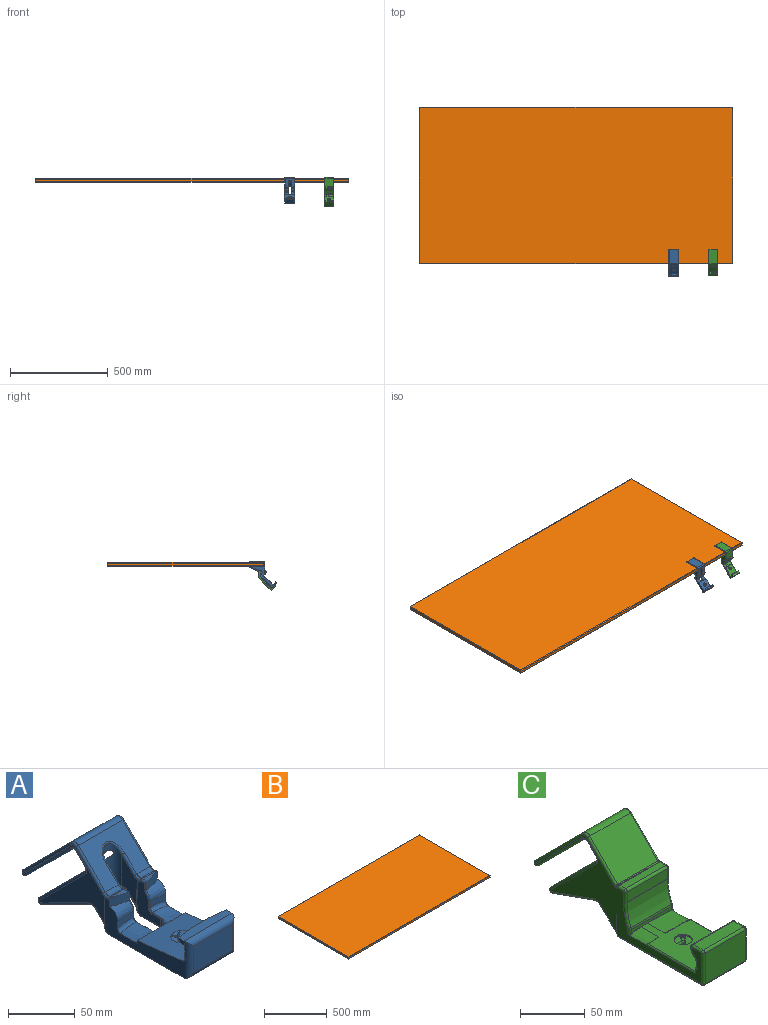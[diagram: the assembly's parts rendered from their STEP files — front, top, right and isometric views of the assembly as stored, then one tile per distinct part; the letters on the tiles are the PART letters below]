
ASSEMBLY  parts=3 mates=2
PART A: 157 faces, bbox 58x178.3x75.5 mm
  f0: plane 46.81x28.52mm, normal (0,-0.71,0.71), area 1310.9mm2, adj f93,f95,f96,f110,f126,f151,f152,f154
  f1: plane 22.07x1.36mm, normal (0,-1,-0.05), area 4.8mm2, adj f3,f60,f61,f104,f141
  f2: plane 13.46x10.49mm, normal (0,0.71,-0.71), area 199.8mm2, adj f4,f13,f140,f141
  f3: bspline ~5.22x5.21mm, area 0.6mm2, adj f1,f60,f104,f148,f149,f150
  f4: cylinder r=5mm len=13.6mm, axis (-1,0,0), area 84mm2, adj f2,f84,f139,f142,f143
  f5: cylinder r=3mm len=18.91mm, axis (1,0,0), area 89.1mm2, adj f86,f87,f103,f117
  f6: extruded ~23.2x17.5mm, area 327.6mm2, adj f14,f26,f31,f32,f46,f50,f80,f82
  f7: plane 14.8x4.53mm, normal (0,0,1), area 40.9mm2, adj f8,f12,f125,f148
  f8: cylinder r=64.23mm len=16.24mm, axis (0,0,-1), area 138mm2, adj f7,f10,f27,f64,f125,f148
  f9: plane 16.39x7.94mm, normal (0,-1,0), area 91.5mm2, adj f10,f11,f27,f68
  f10: bspline ~24.3x9.47mm, area 179.2mm2, adj f8,f9,f27,f64,f66
  f11: bspline ~21.12x6.05mm, area 78.8mm2, adj f9,f27,f30,f70
  f12: cylinder r=5mm len=14.56mm, axis (1,0,0), area 18.3mm2, adj f7,f95,f125,f149
  f13: cylinder r=5mm len=16.38mm, axis (-1,0,0), area 129.8mm2, adj f2,f25,f27,f61,f62,f140,f141
  f14: extruded ~50.8x50.75mm, area 2434.9mm2, adj f6,f15,f16,f17,f24,f26,f27,f28
  f15: extruded ~11.38x4.58mm, area 51.7mm2, adj f14,f16,f25,f55,f57
  f16: extruded ~11.38x4.58mm, area 51.7mm2, adj f14,f15,f25,f54,f57
  f17: extruded ~11.41x3.75mm, area 45.5mm2, adj f14,f18,f25,f54,f56
  f18: extruded ~10.43x9mm, area 95.8mm2, adj f17,f19,f25,f56
  f19: cylinder r=7.6mm len=10.43mm, axis (0,0,1), area 5mm2, adj f18,f20,f25,f56
  f20: extruded ~10.4x7.96mm, area 89.4mm2, adj f19,f21,f25,f56
  f21: extruded ~10.4x7.96mm, area 89.4mm2, adj f20,f22,f25,f56
  f22: cylinder r=7.6mm len=10.43mm, axis (0,0,1), area 5mm2, adj f21,f23,f25,f56
  f23: extruded ~10.43x9mm, area 95.8mm2, adj f22,f24,f25,f56
  f24: extruded ~11.41x3.75mm, area 45.5mm2, adj f14,f23,f25,f55,f56
  f25: plane 79x50.8mm, normal (0,0,-1), area 3479.4mm2, adj f13,f15,f16,f17,f18,f19,f20,f21
  f26: plane 84.61x32.41mm, normal (1,0,0), area 1122.5mm2, adj f6,f14,f25,f29,f31,f44,f45,f49
  f27: plane 84.61x32.68mm, normal (-1,0,0), area 1124.1mm2, adj f8,f9,f10,f11,f13,f14,f25,f28
  f28: cylinder r=5mm len=34mm, axis (0,0,-1), area 229mm2, adj f14,f27,f36,f38,f39,f40,f41,f42
  f29: cylinder r=5mm len=34mm, axis (0,0,1), area 230mm2, adj f14,f26,f35,f38,f39,f40,f41,f42
  f30: extruded ~23.06x17.5mm, area 322.8mm2, adj f11,f14,f27,f32,f33,f48,f72,f73
  f31: plane 12.47x2.53mm, normal (0,1,0), area 9.5mm2, adj f6,f14,f26
  f32: plane 19.29x7.26mm, normal (0,1,0), area 76.8mm2, adj f6,f14,f30,f78
  f33: plane 12.3x2.44mm, normal (0,1,0), area 9.3mm2, adj f14,f27,f30
  f34: plane 13.6x4.54mm, normal (0,0,1), area 40.4mm2, adj f44,f51,f106,f153
  f35: plane 6.51x4.26mm, normal (1,0,0), area 20mm2, adj f29,f37,f38,f43
  f36: plane 6.55x4.26mm, normal (-1,0,0), area 20.2mm2, adj f28,f37,f38,f43
  f37: plane 50.8x8.41mm, normal (0,0,1), area 390.9mm2, adj f35,f36,f41,f43
  f38: plane 50.8x4.13mm, normal (0,0,-1), area 65.1mm2, adj f28,f29,f35,f36,f42,f43
  f39: plane 40.8x24mm, normal (0,-1,0), area 979.2mm2, adj f28,f29,f40,f41
  f40: cylinder r=5mm len=50.8mm, axis (1,0,0), area 359.7mm2, adj f25,f28,f29,f39
  f41: cylinder r=5mm len=50.8mm, axis (-1,0,0), area 359.7mm2, adj f28,f29,f37,f39
  f42: cylinder r=105.29mm len=50.73mm, axis (0,0,-1), area 518.6mm2, adj f28,f29,f38,f47,f53
  f43: torus R=147.23mm, axis (0,0,1), area 350.7mm2, adj f35,f36,f37,f38
  f44: cylinder r=64.23mm len=16.38mm, axis (0,0,-1), area 138.9mm2, adj f26,f34,f49,f75,f106,f153
  f45: plane 16.54x8.04mm, normal (0,-1,0), area 92.4mm2, adj f26,f49,f50,f79
  f46: plane 4.06x0.18mm, normal (0,-1,0), area 0.2mm2, adj f6,f14
  f47: plane 35.45x1.5mm, normal (0,0,-1), area 35.6mm2, adj f42,f53
  f48: plane 3.97x0.13mm, normal (0,-1,0), area 0.2mm2, adj f14,f30
  f49: bspline ~22.57x10.34mm, area 180.9mm2, adj f26,f44,f45,f75,f77
  f50: bspline ~20.53x5.8mm, area 79.7mm2, adj f6,f26,f45,f81
  f51: cylinder r=5mm len=13.6mm, axis (1,0,0), area 17.8mm2, adj f34,f93,f107,f155
  f52: cylinder r=5mm len=16.52mm, axis (-1,0,0), area 130.9mm2, adj f25,f26,f69,f71,f91,f124,f147
  f53: cylinder r=2mm len=50.73mm, axis (1,0,0), area 146.4mm2, adj f14,f28,f29,f42,f47
  f54: cylinder r=7.6mm len=11.41mm, axis (0,0,1), area 5.8mm2, adj f14,f16,f17,f25
  f55: cylinder r=7.6mm len=11.41mm, axis (0,0,1), area 5.8mm2, adj f14,f15,f24,f25
  f56: sphere r=12.32mm, area 242.2mm2, adj f14,f17,f18,f19,f20,f21,f22,f23
  f57: sphere r=12.32mm, area 14.4mm2, adj f14,f15,f16
  f58: plane 31.56x24.67mm, normal (-1,0,0), area 419.9mm2, adj f59,f67,f69,f71,f75,f77,f79,f81
  f59: cylinder r=7.95mm len=15.91mm, axis (0,0,1), area 104.9mm2, adj f58,f60,f65,f73,f76,f78,f80
  f60: plane 31.57x24.52mm, normal (1,0,0), area 419.3mm2, adj f1,f3,f59,f61,f62,f63,f64,f66
  f61: cylinder r=1mm len=18.79mm, axis (0,0,-1), area 10.8mm2, adj f1,f13,f60,f62,f141
  f62: torus R=4mm, axis (1,0,0), area 11.3mm2, adj f13,f60,f61,f63
  f63: cylinder r=1mm len=20.52mm, axis (0,-1,0), area 32.2mm2, adj f25,f60,f62,f65
  f64: cylinder r=1mm len=8.61mm, axis (0,0,-1), area 13mm2, adj f8,f10,f60,f66,f148
  f65: torus R=8.95mm, axis (0,0,-1), area 41.3mm2, adj f25,f59,f63,f67
  f66: bspline ~10.43x6.27mm, area 14.2mm2, adj f10,f60,f64,f68
  f67: cylinder r=1mm len=20.67mm, axis (0,1,0), area 32.5mm2, adj f25,f58,f65,f69
  f68: cylinder r=1mm len=5.89mm, axis (0,0,1), area 9.3mm2, adj f9,f60,f66,f70
  f69: torus R=4mm, axis (1,0,0), area 11.3mm2, adj f52,f58,f67,f71
  f70: bspline ~4.97x4.87mm, area 7.7mm2, adj f11,f60,f68,f72
  f71: cylinder r=1mm len=18.79mm, axis (0,0,1), area 10.8mm2, adj f52,f58,f69,f90,f147
  f72: cylinder r=1mm len=8.77mm, axis (0,-1,0), area 11.1mm2, adj f30,f60,f70,f73
  f73: bspline ~3.21x1.13mm, area 3.2mm2, adj f30,f59,f72,f74
  f74: bspline ~0.78x0.33mm, area 0mm2, adj f30,f73,f76
  f75: cylinder r=1mm len=8.61mm, axis (0,0,-1), area 13mm2, adj f44,f49,f58,f77,f153
  f76: bspline ~7.06x6.68mm, area 10.2mm2, adj f30,f59,f74,f78
  f77: bspline ~10.43x6.27mm, area 14.2mm2, adj f49,f58,f75,f79
  f78: bspline ~5.28x1.44mm, area 5.8mm2, adj f32,f59,f76,f80
  f79: cylinder r=1mm len=5.9mm, axis (0,0,-1), area 9.3mm2, adj f45,f58,f77,f81
  f80: bspline ~9.19x7.2mm, area 13.4mm2, adj f6,f59,f78,f82
  f81: bspline ~5.03x4.86mm, area 7.5mm2, adj f50,f58,f79,f82
  f82: cylinder r=1mm len=8.92mm, axis (0,-1,0), area 10.5mm2, adj f6,f58,f80,f81
  f83: plane 87.64x70.47mm, normal (1,0,0), area 1316.6mm2, adj f26,f109,f110,f111,f112,f113,f114,f115
  f84: plane 51.38x46.81mm, normal (0,-0.44,-0.9), area 2551.5mm2, adj f4,f97,f98,f122,f138,f144
  f85: plane 46.81x0.5mm, normal (0,0.71,-0.71), area 32.9mm2, adj f98,f99,f120,f136
  f86: plane 49.14x49.14mm, normal (0,0.71,0.71), area 3240.2mm2, adj f5,f99,f101,f103,f118,f134
  f87: plane 46.81x9.19mm, normal (0,0.71,-0.71), area 595.7mm2, adj f5,f101,f102,f103,f116,f132
  f88: plane 49.14x49.14mm, normal (0,-0.71,-0.71), area 3252.9mm2, adj f100,f102,f114,f130
  f89: plane 51.27x51.27mm, normal (0,0.71,0.71), area 3393.4mm2, adj f96,f100,f112,f128
  f90: plane 22.07x1.35mm, normal (0,-1,-0.05), area 4.8mm2, adj f58,f71,f94,f105,f147
  f91: plane 13.6x10.49mm, normal (0,0.71,-0.71), area 201.8mm2, adj f52,f97,f124,f147
  f92: plane 87.63x70.47mm, normal (-1,0,0), area 1316.6mm2, adj f27,f125,f126,f127,f128,f129,f130,f131
  f93: cylinder r=5mm len=13.6mm, axis (1,0,0), area 71.2mm2, adj f0,f51,f108,f109,f156
  f94: bspline ~5.21x5.19mm, area 0.6mm2, adj f58,f90,f105,f153,f155,f156
  f95: cylinder r=5mm len=13.46mm, axis (1,0,0), area 70.5mm2, adj f0,f12,f125,f150
  f96: cylinder r=5mm len=46.81mm, axis (-1,0,0), area 367.6mm2, adj f0,f89,f111,f127
  f97: cylinder r=5mm len=13.75mm, axis (-1,0,0), area 84.9mm2, adj f84,f91,f123,f145,f146
  f98: cylinder r=2.5mm len=46.81mm, axis (-1,0,0), area 145.9mm2, adj f84,f85,f121,f137
  f99: cylinder r=2.5mm len=46.81mm, axis (-1,0,0), area 183.8mm2, adj f85,f86,f119,f135
  f100: cylinder r=2.5mm len=46.81mm, axis (1,0,0), area 367.6mm2, adj f88,f89,f113,f129
  f101: cylinder r=3mm len=18.77mm, axis (1,0,0), area 88.4mm2, adj f86,f87,f103,f133
  f102: cylinder r=3mm len=46.81mm, axis (1,0,0), area 220.6mm2, adj f87,f88,f115,f131
  f103: cylinder r=7.87mm len=42.38mm, axis (0,0,-1), area 853.5mm2, adj f5,f86,f87,f101,f104,f105,f143,f144
  f104: plane 38.69x19.09mm, normal (1,0,0), area 387.2mm2, adj f1,f3,f103,f141,f142,f143,f150,f151
  f105: plane 38.94x19.33mm, normal (-1,0,0), area 394.1mm2, adj f90,f94,f103,f146,f147,f154,f156
  f106: cylinder r=2mm len=2mm, axis (0,-1,0), area 1.1mm2, adj f26,f34,f44,f107
  f107: torus R=3mm, axis (-1,0,0), area 3.5mm2, adj f26,f51,f106,f108
  f108: torus R=7mm, axis (-1,0,0), area 8.7mm2, adj f26,f93,f107,f109
  f109: torus R=7mm, axis (1,0,0), area 10.2mm2, adj f83,f93,f108,f110
  f110: cylinder r=2mm len=29.94mm, axis (0,0.71,0.71), area 126.7mm2, adj f0,f83,f109,f111
  f111: torus R=3mm, axis (1,0,0), area 21.1mm2, adj f83,f96,f110,f112
  f112: cylinder r=2mm len=52.68mm, axis (0,0.71,-0.71), area 227.8mm2, adj f83,f89,f111,f113
  f113: torus R=0.5mm, axis (1,0,0), area 17.5mm2, adj f83,f100,f112,f114
  f114: cylinder r=2mm len=50.56mm, axis (0,-0.71,0.71), area 218.3mm2, adj f83,f88,f113,f115
  f115: torus R=5mm, axis (1,0,0), area 18.4mm2, adj f83,f102,f114,f116
  f116: cylinder r=2mm len=10.61mm, axis (0,-0.71,-0.71), area 40.8mm2, adj f83,f87,f115,f117
  f117: torus R=5mm, axis (1,0,0), area 18.4mm2, adj f5,f83,f116,f118
  f118: cylinder r=2mm len=50.56mm, axis (0,0.71,-0.71), area 218.3mm2, adj f83,f86,f117,f119
  f119: torus R=0.5mm, axis (1,0,0), area 8.8mm2, adj f83,f99,f118,f120
  f120: cylinder r=2mm len=2mm, axis (0,-0.71,-0.71), area 2.2mm2, adj f83,f85,f119,f121
  f121: torus R=0.5mm, axis (1,0,0), area 6.9mm2, adj f83,f98,f120,f122
  f122: cylinder r=2mm len=52.27mm, axis (0,-0.9,0.44), area 180.2mm2, adj f83,f84,f121,f123
  f123: torus R=7mm, axis (1,0,0), area 22.4mm2, adj f83,f97,f122,f124
  f124: cylinder r=2mm len=11.91mm, axis (0,-0.71,-0.71), area 44.6mm2, adj f26,f52,f83,f91,f123
  f125: torus R=7mm, axis (1,0,0), area 22.1mm2, adj f7,f8,f12,f27,f92,f95,f126
  f126: cylinder r=2mm len=29.94mm, axis (0,-0.71,-0.71), area 126.7mm2, adj f0,f92,f125,f127
  f127: torus R=3mm, axis (1,0,0), area 21.1mm2, adj f92,f96,f126,f128
  f128: cylinder r=2mm len=52.68mm, axis (0,-0.71,0.71), area 227.8mm2, adj f89,f92,f127,f129
  f129: torus R=0.5mm, axis (1,0,0), area 17.5mm2, adj f92,f100,f128,f130
  f130: cylinder r=2mm len=50.56mm, axis (0,0.71,-0.71), area 218.3mm2, adj f88,f92,f129,f131
  f131: torus R=5mm, axis (1,0,0), area 18.4mm2, adj f92,f102,f130,f132
  f132: cylinder r=2mm len=10.61mm, axis (0,0.71,0.71), area 40.8mm2, adj f87,f92,f131,f133
  f133: torus R=5mm, axis (1,0,0), area 18.4mm2, adj f92,f101,f132,f134
  f134: cylinder r=2mm len=50.56mm, axis (0,-0.71,0.71), area 218.3mm2, adj f86,f92,f133,f135
  f135: torus R=0.5mm, axis (1,0,0), area 8.8mm2, adj f92,f99,f134,f136
  f136: cylinder r=2mm len=2mm, axis (0,0.71,0.71), area 2.2mm2, adj f85,f92,f135,f137
  f137: torus R=0.5mm, axis (1,0,0), area 6.9mm2, adj f92,f98,f136,f138
  f138: cylinder r=2mm len=52.27mm, axis (0,0.9,-0.44), area 180.2mm2, adj f84,f92,f137,f139
  f139: torus R=7mm, axis (1,0,0), area 22.4mm2, adj f4,f92,f138,f140
  f140: cylinder r=2mm len=11.91mm, axis (0,0.71,0.71), area 44.7mm2, adj f2,f13,f27,f92,f139
  f141: cylinder r=2mm len=11.91mm, axis (0,-0.71,-0.71), area 44.4mm2, adj f1,f2,f13,f61,f104,f142
  f142: torus R=7mm, axis (1,0,0), area 17.1mm2, adj f4,f104,f141,f143
  f143: bspline ~3.89x3.13mm, area 4.6mm2, adj f4,f103,f104,f142,f144
  f144: bspline ~19.46x8.22mm, area 65.2mm2, adj f84,f103,f143,f145
  f145: bspline ~3.77x3.13mm, area 3.9mm2, adj f97,f103,f144,f146
  f146: torus R=7mm, axis (1,0,0), area 17.8mm2, adj f97,f105,f145,f147
  f147: cylinder r=2mm len=11.91mm, axis (0,0.71,0.71), area 44.4mm2, adj f52,f71,f90,f91,f105,f146
  f148: cylinder r=2mm len=4.66mm, axis (0,1,0), area 11.5mm2, adj f3,f7,f8,f60,f64,f149
  f149: torus R=3mm, axis (1,0,0), area 3.3mm2, adj f3,f12,f148,f150
  f150: torus R=7mm, axis (1,0,0), area 18.8mm2, adj f3,f95,f104,f149,f151
  f151: cylinder r=2mm len=14.07mm, axis (0,0.71,0.71), area 56.2mm2, adj f0,f104,f150,f152
  f152: bspline ~19.75x13mm, area 79.3mm2, adj f0,f103,f104,f151,f154
  f153: cylinder r=2mm len=4.67mm, axis (0,-1,0), area 11.5mm2, adj f34,f44,f58,f75,f94,f155
  f154: cylinder r=2mm len=14.33mm, axis (0,-0.71,-0.71), area 57.4mm2, adj f0,f105,f152,f156
  f155: torus R=3mm, axis (1,0,0), area 3.3mm2, adj f51,f94,f153,f156
  f156: torus R=7mm, axis (1,0,0), area 18.8mm2, adj f93,f94,f105,f154,f155
PART B: 26 faces, bbox 1600x800x19 mm
  f0: plane 1594x13mm, normal (0,1,0), area 20722mm2, adj f14,f19,f22,f25
  f1: plane 794x13mm, normal (-1,0,0), area 10322mm2, adj f11,f20,f21,f25
  f2: plane 1594x13mm, normal (0,-1,0), area 20722mm2, adj f6,f10,f11,f12
  f3: plane 794x13mm, normal (1,0,0), area 10322mm2, adj f6,f9,f13,f14
  f4: plane 1594x794mm, normal (0,0,1), area 1265636mm2, adj f9,f10,f19,f20
  f5: plane 1594x794mm, normal (0,0,-1), area 1265636mm2, adj f12,f13,f21,f22
  f6: cylinder r=3mm len=13mm, axis (0,0,1), area 61.3mm2, adj f2,f3,f7,f8
  f7: sphere r=3mm, area 14.1mm2, adj f6,f9,f10
  f8: sphere r=3mm, area 14.1mm2, adj f6,f12,f13
  f9: cylinder r=3mm len=794mm, axis (0,-1,0), area 3741.6mm2, adj f3,f4,f7,f15
  f10: cylinder r=3mm len=1594mm, axis (-1,0,0), area 7511.5mm2, adj f2,f4,f7,f16
  f11: cylinder r=3mm len=13mm, axis (0,0,-1), area 61.3mm2, adj f1,f2,f16,f17
  f12: cylinder r=3mm len=1594mm, axis (1,0,0), area 7511.5mm2, adj f2,f5,f8,f17
  f13: cylinder r=3mm len=794mm, axis (0,1,0), area 3741.6mm2, adj f3,f5,f8,f18
  f14: cylinder r=3mm len=13mm, axis (0,0,-1), area 61.3mm2, adj f0,f3,f15,f18
  f15: sphere r=3mm, area 14.1mm2, adj f9,f14,f19
  f16: sphere r=3mm, area 14.1mm2, adj f10,f11,f20
  f17: sphere r=3mm, area 14.1mm2, adj f11,f12,f21
  f18: sphere r=3mm, area 14.1mm2, adj f13,f14,f22
  f19: cylinder r=3mm len=1594mm, axis (1,0,0), area 7511.5mm2, adj f0,f4,f15,f23
  f20: cylinder r=3mm len=794mm, axis (0,1,0), area 3741.6mm2, adj f1,f4,f16,f23
  f21: cylinder r=3mm len=794mm, axis (0,-1,0), area 3741.6mm2, adj f1,f5,f17,f24
  f22: cylinder r=3mm len=1594mm, axis (-1,0,0), area 7511.5mm2, adj f0,f5,f18,f24
  f23: sphere r=3mm, area 14.1mm2, adj f19,f20,f25
  f24: sphere r=3mm, area 14.1mm2, adj f21,f22,f25
  f25: cylinder r=3mm len=13mm, axis (0,0,1), area 61.3mm2, adj f0,f1,f23,f24
PART C: 152 faces, bbox 49.5x185.6x80.7 mm
  f0: cylinder r=2mm len=45.04mm, axis (-1,0,0), area 43.4mm2, adj f6,f66,f69,f111,f141,f151
  f1: plane 43.83x2.19mm, normal (0,1,0), area 96.1mm2, adj f29,f47,f53,f56
  f2: plane 93.01x44.56mm, normal (1,0,0), area 1119.8mm2, adj f11,f12,f13,f20,f21,f23,f26,f34
  f3: plane 93x44.55mm, normal (-1,0,0), area 1142.3mm2, adj f14,f15,f16,f18,f19,f22,f26,f43
  f4: plane 43.83x28.98mm, normal (0,-1,0), area 1270mm2, adj f41,f42,f49,f50
  f5: extruded ~71.8x46.09mm, area 2417.4mm2, adj f9,f10,f12,f13,f14,f15,f18,f19
  f6: plane 43.83x6.31mm, normal (0,0,1), area 276.7mm2, adj f0,f66,f69,f70
  f7: plane 91x43.83mm, normal (0,0,-1), area 3988.2mm2, adj f36,f39,f42,f43
  f8: plane 43.83x0.05mm, normal (0,1,0), area 2.4mm2, adj f39,f110,f115,f127
  f9: plane 45.9x3.61mm, normal (0,1,0), area 133.9mm2, adj f5,f26,f77,f78
  f10: plane 43.9x3.29mm, normal (0,-1,0), area 118.1mm2, adj f5,f32,f62,f76
  f11: plane 1.61x1.13mm, normal (0,1,0), area 0.6mm2, adj f2,f13,f21
  f12: plane 28.53x3.08mm, normal (0,-1,0), area 4.6mm2, adj f2,f5,f13,f23
  f13: extruded ~28.45x19.1mm, area 539.2mm2, adj f2,f5,f11,f12,f21
  f14: extruded ~19.1x12.61mm, area 241.5mm2, adj f3,f5,f15,f16,f19
  f15: plane 12.68x1.87mm, normal (0,-1,0), area 1.6mm2, adj f3,f5,f14,f22
  f16: plane 0.06x0.04mm, normal (0,1,0), area 0mm2, adj f3,f14,f19
  f17: plane 43.83x9.55mm, normal (0,-1,0), area 418.6mm2, adj f33,f67,f70,f72
  f18: cylinder r=1mm len=53.99mm, axis (0,1,0), area 78.3mm2, adj f3,f5,f19,f77
  f19: bspline ~15.28x1.96mm, area 4.5mm2, adj f3,f5,f14,f16,f18
  f20: cylinder r=1mm len=53.98mm, axis (0,1,0), area 74mm2, adj f2,f5,f21,f78
  f21: bspline ~30.38x2.21mm, area 12.8mm2, adj f2,f5,f11,f13,f20
  f22: cylinder r=1mm len=2.3mm, axis (0,1,0), area 2.2mm2, adj f3,f5,f15,f76
  f23: cylinder r=1mm len=2.3mm, axis (0,1,0), area 2.1mm2, adj f2,f5,f12,f62
  f24: cylinder r=5.5mm len=43.83mm, axis (-1,0,0), area 303.8mm2, adj f25,f28,f35,f60
  f25: plane 43.83x5.31mm, normal (0,1,0), area 232.7mm2, adj f24,f26,f34,f61
  f26: plane 47.83x2.2mm, normal (0,0,1), area 10.7mm2, adj f2,f3,f9,f25,f34,f61,f77,f78
  f27: plane 43.83x3.94mm, normal (0,0.93,-0.36), area 184.6mm2, adj f28,f29,f40,f58
  f28: cylinder r=1mm len=43.83mm, axis (-1,0,0), area 39.3mm2, adj f24,f27,f37,f59
  f29: cylinder r=1mm len=43.83mm, axis (1,0,0), area 16mm2, adj f1,f27,f44,f57
  f30: plane 43.83x10.72mm, normal (0,0,1), area 469.8mm2, adj f48,f49,f53,f54
  f31: extruded ~43.83x21.6mm, area 970.8mm2, adj f32,f33,f64,f74
  f32: cylinder r=5mm len=43.83mm, axis (-1,0,0), area 83mm2, adj f10,f31,f63,f75
  f33: cylinder r=5mm len=43.83mm, axis (-1,0,0), area 17.5mm2, adj f17,f31,f65,f73
  f34: cylinder r=2mm len=5.31mm, axis (0,0,1), area 16.7mm2, adj f2,f25,f26,f35
  f35: torus R=7.5mm, axis (1,0,0), area 24mm2, adj f2,f24,f34,f37
  f36: cylinder r=2mm len=91mm, axis (0,-1,0), area 285.9mm2, adj f2,f7,f38,f114
  f37: bspline ~2.46x1.74mm, area 1.2mm2, adj f28,f35,f40
  f38: sphere r=2mm, area 6.3mm2, adj f36,f41,f42
  f39: cylinder r=2mm len=43.83mm, axis (1,0,0), area 137.7mm2, adj f7,f8,f114,f128
  f40: cylinder r=2mm len=4.65mm, axis (0,-0.36,-0.93), area 12.2mm2, adj f2,f27,f37,f44
  f41: cylinder r=2mm len=28.98mm, axis (0,0,-1), area 91mm2, adj f2,f4,f38,f45
  f42: cylinder r=2mm len=43.83mm, axis (-1,0,0), area 137.7mm2, adj f4,f7,f38,f46
  f43: cylinder r=2mm len=91mm, axis (0,1,0), area 285.9mm2, adj f3,f7,f46,f128
  f44: bspline ~2.27x2mm, area 0.5mm2, adj f29,f40,f47
  f45: sphere r=2mm, area 6.3mm2, adj f41,f48,f49
  f46: sphere r=2mm, area 6.3mm2, adj f42,f43,f50
  f47: cylinder r=2mm len=2.19mm, axis (0,0,1), area 6.6mm2, adj f1,f2,f44,f51
  f48: cylinder r=2mm len=10.72mm, axis (0,-1,0), area 33.7mm2, adj f2,f30,f45,f51
  f49: cylinder r=2mm len=43.83mm, axis (-1,0,0), area 137.7mm2, adj f4,f30,f45,f52
  f50: cylinder r=2mm len=28.98mm, axis (0,0,1), area 91mm2, adj f3,f4,f46,f52
  f51: sphere r=2mm, area 4mm2, adj f47,f48,f53
  f52: sphere r=2mm, area 6.3mm2, adj f49,f50,f54
  f53: cylinder r=2mm len=43.83mm, axis (1,0,0), area 137.7mm2, adj f1,f30,f51,f55
  f54: cylinder r=2mm len=10.72mm, axis (0,1,0), area 33.7mm2, adj f3,f30,f52,f55
  f55: sphere r=2mm, area 8.6mm2, adj f53,f54,f56
  f56: cylinder r=2mm len=2.19mm, axis (0,0,-1), area 6.6mm2, adj f1,f3,f55,f57
  f57: bspline ~2.07x2mm, area 0.5mm2, adj f29,f56,f58
  f58: cylinder r=2mm len=4.65mm, axis (0,-0.36,-0.93), area 12.2mm2, adj f3,f27,f57,f59
  f59: bspline ~2.46x1.74mm, area 1.2mm2, adj f28,f58,f60
  f60: torus R=7.5mm, axis (1,0,0), area 24mm2, adj f3,f24,f59,f61
  f61: cylinder r=2mm len=5.31mm, axis (0,0,-1), area 16.7mm2, adj f3,f25,f26,f60
  f62: cylinder r=2mm len=4.39mm, axis (0,0,-1), area 11.5mm2, adj f2,f5,f10,f23,f63
  f63: torus R=3mm, axis (1,0,0), area 5.1mm2, adj f2,f32,f62,f64
  f64: bspline ~23.34x6.36mm, area 70.6mm2, adj f2,f31,f63,f65
  f65: torus R=3mm, axis (1,0,0), area 1.1mm2, adj f2,f33,f64,f67
  f66: cylinder r=2mm len=6.92mm, axis (0,1,0), area 20.8mm2, adj f0,f2,f6,f68,f141
  f67: cylinder r=2mm len=9.55mm, axis (0,0,1), area 30mm2, adj f2,f17,f65,f68
  f68: sphere r=2mm, area 6.3mm2, adj f66,f67,f70
  f69: cylinder r=2mm len=6.92mm, axis (0,-1,0), area 20.8mm2, adj f0,f3,f6,f71,f151
  f70: cylinder r=2mm len=43.83mm, axis (1,0,0), area 137.7mm2, adj f6,f17,f68,f71
  f71: sphere r=2mm, area 6.3mm2, adj f69,f70,f72
  f72: cylinder r=2mm len=9.55mm, axis (0,0,-1), area 30mm2, adj f3,f17,f71,f73
  f73: torus R=3mm, axis (1,0,0), area 1.1mm2, adj f3,f33,f72,f74
  f74: bspline ~24.18x6.56mm, area 70.6mm2, adj f3,f31,f73,f75
  f75: torus R=3mm, axis (1,0,0), area 5.1mm2, adj f3,f32,f74,f76
  f76: cylinder r=2mm len=4.3mm, axis (0,0,1), area 11.3mm2, adj f3,f5,f10,f22,f75
  f77: cylinder r=1mm len=4.5mm, axis (0,0,-1), area 6.1mm2, adj f3,f5,f9,f18,f26
  f78: cylinder r=1mm len=4.59mm, axis (0,0,1), area 6.2mm2, adj f2,f5,f9,f20,f26
  f79: cylinder r=7mm len=14mm, axis (0,0,1), area 44.2mm2, adj f5,f80,f86,f87
  f80: plane 3.92x1.22mm, normal (0.12,0.99,0), area 4.5mm2, adj f5,f79,f81,f87
  f81: cylinder r=1.76mm len=1.55mm, axis (0,0,1), area 2mm2, adj f5,f80,f82,f87
  f82: plane 3.28x2.66mm, normal (-0.78,0.63,0), area 5.2mm2, adj f5,f81,f83,f87
  f83: cylinder r=1.96mm len=3.92mm, axis (0,0,1), area 11.6mm2, adj f5,f82,f84,f87
  f84: plane 3.4x2.95mm, normal (0.65,-0.76,0), area 5.5mm2, adj f5,f83,f85,f87
  f85: cylinder r=1.76mm len=3.16mm, axis (0,0,1), area 5.8mm2, adj f5,f84,f86,f87
  f86: plane 3.17x1.21mm, normal (-0.12,-0.99,0), area 3.6mm2, adj f5,f79,f85,f87
  f87: plane 14x14mm, normal (0,0,1), area 115.8mm2, adj f79,f80,f81,f82,f83,f84,f85,f86
  f88: cylinder r=1.06mm len=2.11mm, axis (0,0,1), area 8mm2, adj f90,f91
  f89: cylinder r=1.34mm len=2.69mm, axis (0,0,1), area 10.1mm2, adj f5,f90
  f90: plane 2.69x2.69mm, normal (0,0,1), area 2.2mm2, adj f88,f89
  f91: extruded ~2.11x2.11mm, area 3.5mm2, adj f88
  f92: plane 1.26x1.01mm, normal (-0.12,-0.99,0), area 1.2mm2, adj f5,f93,f95,f96
  f93: cylinder r=1.58mm len=3.17mm, axis (0,0,1), area 8.7mm2, adj f5,f92,f94,f96
  f94: plane 1.26x1.01mm, normal (0.12,0.99,0), area 1.2mm2, adj f5,f93,f95,f96
  f95: cylinder r=1.22mm len=2.43mm, axis (0,0,1), area 4.8mm2, adj f5,f92,f94,f96
  f96: plane 3.17x2.73mm, normal (0,0,1), area 2.1mm2, adj f92,f93,f94,f95
  f97: plane 43.83x18.48mm, normal (0,0.69,-0.72), area 1123.6mm2, adj f108,f110,f117,f118,f124,f125
  f98: plane 43.82x30.32mm, normal (0,-0.71,0.71), area 1879mm2, adj f109,f111,f143,f149
  f99: plane 44.92x43.82mm, normal (0,-0.34,-0.94), area 2089.1mm2, adj f108,f120,f121,f122
  f100: plane 47.83x1.24mm, normal (0,0.71,-0.71), area 82.9mm2, adj f106,f107,f120,f121,f122,f131
  f101: plane 49.5x49.5mm, normal (0,0.71,0.71), area 3067.4mm2, adj f112,f129,f131,f133
  f102: plane 43.82x9.19mm, normal (0,0.71,-0.71), area 569.7mm2, adj f112,f113,f132,f137
  f103: plane 49.5x49.5mm, normal (0,-0.71,-0.71), area 3067.4mm2, adj f113,f136,f138,f140
  f104: plane 47.82x0.71mm, normal (0,0.71,-0.71), area 47.8mm2, adj f106,f107,f138,f146
  f105: plane 51.62x51.62mm, normal (0,0.71,0.71), area 3198.9mm2, adj f109,f145,f146,f147
  f106: plane 89.14x73.03mm, normal (1,0,0), area 1833.4mm2, adj f2,f100,f104,f118,f119,f120,f133,f135
  f107: plane 89.13x73.02mm, normal (-1,0,0), area 1833.4mm2, adj f3,f100,f104,f122,f123,f124,f129,f130
  f108: cylinder r=5mm len=43.82mm, axis (1,0,0), area 242.7mm2, adj f97,f99,f119,f123
  f109: cylinder r=5mm len=43.82mm, axis (-1,0,0), area 344.2mm2, adj f98,f105,f144,f148
  f110: cylinder r=1mm len=43.83mm, axis (1,0,0), area 35.3mm2, adj f8,f97,f116,f126
  f111: cylinder r=1mm len=43.83mm, axis (-1,0,0), area 55.8mm2, adj f0,f98,f141,f142,f150,f151
  f112: cylinder r=3mm len=43.82mm, axis (1,0,0), area 206.5mm2, adj f101,f102,f130,f135
  f113: cylinder r=3mm len=43.82mm, axis (1,0,0), area 206.5mm2, adj f102,f103,f134,f139
  f114: sphere r=2mm, area 4mm2, adj f36,f39,f115
  f115: cylinder r=2mm len=2mm, axis (0,0,1), area 0.2mm2, adj f2,f8,f114,f116
  f116: torus R=3mm, axis (1,0,0), area 4.4mm2, adj f2,f110,f115,f117
  f117: cylinder r=2mm len=2.48mm, axis (0,-0.72,-0.69), area 4.7mm2, adj f2,f97,f116,f118
  f118: cylinder r=2mm len=18.78mm, axis (0,-0.72,-0.69), area 75.8mm2, adj f97,f106,f117,f119
  f119: torus R=7mm, axis (1,0,0), area 19.9mm2, adj f106,f108,f118,f120
  f120: cylinder r=2mm len=47.68mm, axis (0,-0.94,0.34), area 153.6mm2, adj f99,f100,f106,f119,f121
  f121: cylinder r=2mm len=47.43mm, axis (-1,0,0), area 102.8mm2, adj f99,f100,f120,f122
  f122: cylinder r=2mm len=47.68mm, axis (0,0.94,-0.34), area 153.6mm2, adj f99,f100,f107,f121,f123
  f123: torus R=7mm, axis (1,0,0), area 19.9mm2, adj f107,f108,f122,f124
  f124: cylinder r=2mm len=18.78mm, axis (0,0.72,0.69), area 75.8mm2, adj f97,f107,f123,f125
  f125: cylinder r=2mm len=2.48mm, axis (0,0.72,0.69), area 4.7mm2, adj f3,f97,f124,f126
  f126: torus R=3mm, axis (1,0,0), area 4.4mm2, adj f3,f110,f125,f127
  f127: cylinder r=2mm len=2mm, axis (0,0,-1), area 0.2mm2, adj f3,f8,f126,f128
  f128: sphere r=2mm, area 8.6mm2, adj f39,f43,f127
  f129: cylinder r=2mm len=52.33mm, axis (0,-0.71,0.71), area 223.1mm2, adj f101,f107,f130,f131
  f130: torus R=5mm, axis (1,0,0), area 18.4mm2, adj f107,f112,f129,f132
  f131: cylinder r=2mm len=47.82mm, axis (-1,0,0), area 143.9mm2, adj f100,f101,f129,f133
  f132: cylinder r=2mm len=10.61mm, axis (0,0.71,0.71), area 40.8mm2, adj f102,f107,f130,f134
  f133: cylinder r=2mm len=52.33mm, axis (0,0.71,-0.71), area 223.1mm2, adj f101,f106,f131,f135
  f134: torus R=5mm, axis (1,0,0), area 18.4mm2, adj f107,f113,f132,f136
  f135: torus R=5mm, axis (1,0,0), area 18.4mm2, adj f106,f112,f133,f137
  f136: cylinder r=2mm len=52.33mm, axis (0,0.71,-0.71), area 223.1mm2, adj f103,f107,f134,f138
  f137: cylinder r=2mm len=10.61mm, axis (0,-0.71,-0.71), area 40.8mm2, adj f102,f106,f135,f139
  f138: cylinder r=2mm len=47.82mm, axis (-1,0,0), area 143.9mm2, adj f103,f104,f136,f140
  f139: torus R=5mm, axis (1,0,0), area 18.4mm2, adj f106,f113,f137,f140
  f140: cylinder r=2mm len=52.33mm, axis (0,-0.71,0.71), area 223.1mm2, adj f103,f106,f138,f139
  f141: torus R=3mm, axis (1,0,0), area 4.5mm2, adj f0,f2,f66,f111,f142
  f142: torus R=3mm, axis (1,0,0), area 3.2mm2, adj f106,f111,f141,f143
  f143: cylinder r=2mm len=31.74mm, axis (0,0.71,0.71), area 134.7mm2, adj f98,f106,f142,f144
  f144: torus R=3mm, axis (1,0,0), area 21.1mm2, adj f106,f109,f143,f145
  f145: cylinder r=2mm len=54.45mm, axis (0,0.71,-0.71), area 232.5mm2, adj f105,f106,f144,f146
  f146: cylinder r=2mm len=47.82mm, axis (-1,0,0), area 143.9mm2, adj f104,f105,f145,f147
  f147: cylinder r=2mm len=54.45mm, axis (0,-0.71,0.71), area 232.5mm2, adj f105,f107,f146,f148
  f148: torus R=3mm, axis (1,0,0), area 21.1mm2, adj f107,f109,f147,f149
  f149: cylinder r=2mm len=31.74mm, axis (0,-0.71,-0.71), area 134.7mm2, adj f98,f107,f148,f150
  f150: torus R=3mm, axis (1,0,0), area 3.2mm2, adj f107,f111,f149,f151
  f151: torus R=3mm, axis (1,0,0), area 4.5mm2, adj f0,f3,f69,f111,f150
PLACE A rot(axis=(1,0,0),45deg) t=(510.44,-447.32,-75.74)mm
PLACE B t=(10.51,-25.8,-8.61)mm
PLACE C rot(axis=(1,0,0),45deg) t=(709.77,-443.96,-90.21)mm
MATE fastened A.f87 <-> B.f2  axis (0,1,0) through (510.51,-425.8,0.89)mm
MATE fastened C.f102 <-> B.f2  axis (0,1,0) through (710.51,-425.8,0.89)mm
